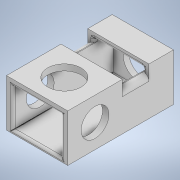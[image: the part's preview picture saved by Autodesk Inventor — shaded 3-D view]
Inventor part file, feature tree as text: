
AUTODESK INVENTOR PART (.ipt)
format: ipt  version: 2020.4 (Build 244396010, 396A)  size: 380,416 bytes
history: native  units: in
note: dims shown in document units (in); Inventor stores cm internally (conversion verified against a paired STEP export)
features: extrude x13, sketch x13, projected_geometry x13, fillet x4
ambient origin geometry x8: Origin, YZ Plane, XZ Plane, XY Plane, X Axis, Y Axis, Z Axis, Center Point
bodies: Solid1 (feature_tree)
feature tree (43):
  extrude  "Extrusion1"  Depth=3.7402in
  extrude  "Extrusion2"  Depth=0.0984in
  extrude  "Extrusion3"  Depth=1.378in
  extrude  "Extrusion4"  Depth=0.8661in
  extrude  "Extrusion5"  Depth=1.811in TaperAngle=0.0deg
  extrude  "Extrusion6"  Depth=0.2362in TaperAngle=0.0deg
  extrude  "Extrusion7"  Depth=0.0984in TaperAngle=0.0deg
  extrude  "Extrusion9"  Depth=0.0197in
  extrude  "Extrusion11"  Depth=0.8563in
  extrude  "Extrusion12"  Depth=0.6693in
  extrude  "Extrusion15"  TaperAngle=180.0deg  [1 undecoded]
  fillet  "Fillet1"  Radius=0.0197in
  fillet  "Fillet3"  Radius=0.0197in
  fillet  "Fillet4"  Radius=0.1181in
  fillet  "Fillet5"  Radius=0.0197in
  extrude  "Extrusion16"  Depth=0.3937in TaperAngle=0.0deg
  extrude  "Extrusion17"  Depth=0.1181in
  sketch  "Sketch1"  dims[d0=1.9685in d1=3.7402in]
  sketch  "Sketch2"  dims[d2=1.5748in d3=0.0in d4=0.0984in]
  projected_geometry  "Projected Loop1"
  sketch  "Sketch3"  dims[d5=1.7717in d6=1.378in]
  projected_geometry  "Projected Loop2"
  sketch  "Sketch4"  dims[d7=3.5433in d8=0.0in d9=0.8661in]
  projected_geometry  "Projected Loop3"
  sketch  "Sketch5"  dims[d10=1.811in d11=0.2362in d12=0.0in]
  projected_geometry  "Projected Loop4"
  sketch  "Sketch6"  dims[d13=0.9843in d14=0.2362in d15=0.0in]
  projected_geometry  "Projected Loop5"
  sketch  "Sketch7"  dims[d16=0.0984in d17=0.0in d18=0.0984in d19=0.0in]
  projected_geometry  "Projected Loop6"
  projected_geometry  "Projected Loop7"
  sketch  "Sketch10"  dims[d20=0.0984in d21=0.0in d29=0.0197in]
  projected_geometry  "Projected Loop9"
  sketch  "Sketch11"  dims[d30=0.0984in d31=0.0in d49=0.8563in]
  projected_geometry  "Projected Loop10"
  sketch  "Sketch12"  dims[d50=0.8563in d51=0.6693in]
  projected_geometry  "Projected Loop11"
  sketch  "Sketch16"  dims[d52=0.3937in d53=0.0in d54=180.0deg d55=0.0197in d56=0.0197in d58=0.1181in d59=0.0197in]
  projected_geometry  "Projected Loop15"
  sketch  "Sketch18"  dims[d60=0.3937in d61=0.0in d66=0.3937in d67=0.0in]
  projected_geometry  "Projected Loop17"
  sketch  "Sketch19"  dims[d68=0.1969in d70=0.1181in d71=0.1181in d73=0.0787in d74=0.9843in d75=0.0in d76=0.0in d77=1.1811in d78=0.3937in d79=0.0in]
  projected_geometry  "Projected Loop18"
note: 1 required parameter value undecoded (feature->parameter linkage not recoverable at this tier; creation-order binding heuristic only, values carry confidence <= 0.55)
